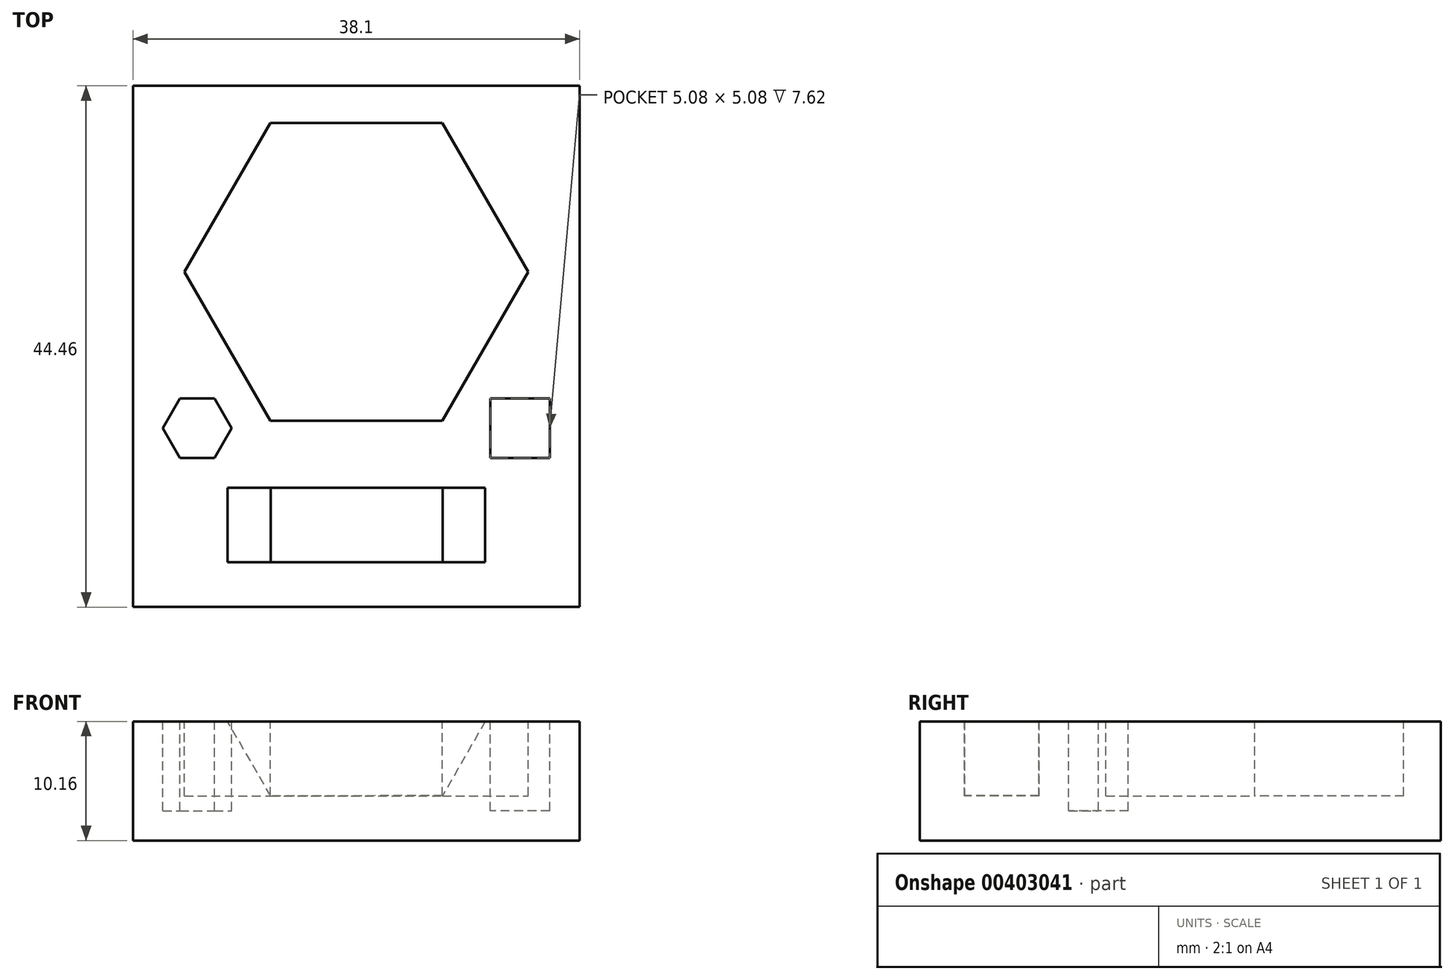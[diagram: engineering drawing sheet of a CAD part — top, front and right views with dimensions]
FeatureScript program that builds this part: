
annotation { "Feature Type Name" : "Feature", "Feature Type Description" : "" }
export const myFeature = defineFeature(function(context is Context, id is Id, definition is map)
    precondition{}
    {
        {
            var Q0;
            Q0=qCreatedBy(makeId("Top.planeOp"),FACE);
            var sketch = newSketch(context, id + "F0", { "sketchPlane" : qUnion([Q0])});
            skLineSegment(sketch, "E0.bottom", {"start": v(19.05, 22.23) * mm, "end": v(-19.05, 22.23) * mm});
            skLineSegment(sketch, "E0.top", {"start": v(19.05, -22.23) * mm, "end": v(-19.05, -22.23) * mm});
            skLineSegment(sketch, "E0.left", {"start": v(19.05, 22.23) * mm, "end": v(19.05, -22.23) * mm});
            skLineSegment(sketch, "E0.right", {"start": v(-19.05, 22.23) * mm, "end": v(-19.05, -22.23) * mm});
            skPoint(sketch, "E0.middle", {"position": v(0, 0) * mm});
            skSolve(sketch);
        }
        {
            var Q0;
            Q0 = qSketchRegion(id + "F0", true);
            extrude(context, id + "F1", {"entities" : qUnion([Q0]), "depth" : 10.16 * mm});
        }
        {
            var Q0;
            Q0=makeQuery(id+"F1.opExtrude","CAP_FACE",FACE,{"disambiguationData":[OSD([sQuery(id+"F0.wireOp",EDGE,"E0.bottom"),sQuery(id+"F0.wireOp",EDGE,"E0.top"),sQuery(id+"F0.wireOp",EDGE,"E0.left"),sQuery(id+"F0.wireOp",EDGE,"E0.right")])],"isStart":false});
            var sketch = newSketch(context, id + "F2", { "sketchPlane" : qUnion([Q0])});
            skCircle(sketch, "E1.cCircle", {"center": v(0, 6.35) * mm, "radius": 12.7 * mm, "construction": true});
            skLineSegment(sketch, "E1.0", {"start": v(7.33, 19.05) * mm, "end": v(14.66, 6.35) * mm});
            skLineSegment(sketch, "E1.1", {"start": v(14.66, 6.35) * mm, "end": v(7.33, -6.35) * mm});
            skLineSegment(sketch, "E1.2", {"start": v(7.33, -6.35) * mm, "end": v(-7.33, -6.35) * mm});
            skLineSegment(sketch, "E1.3", {"start": v(-7.33, -6.35) * mm, "end": v(-14.66, 6.35) * mm});
            skLineSegment(sketch, "E1.4", {"start": v(-14.66, 6.35) * mm, "end": v(-7.33, 19.05) * mm});
            skLineSegment(sketch, "E1.5", {"start": v(-7.33, 19.05) * mm, "end": v(7.33, 19.05) * mm});
            skPoint(sketch, "E1.0.midPoint", {"position": v(11, 12.7) * mm});
            skSolve(sketch);
        }
        {
            var Q0;
            Q0 = qSketchRegion(id + "F2", true);
            extrude(context, id + "F3", {"entities" : qUnion([Q0]), "operationType" : NewBodyOperationType.REMOVE, "oppositeDirection" : true, "depth" : 6.35 * mm});
        }
        {
            var Q0;
            Q0=qCreatedBy(makeId("Front.planeOp"),FACE);
            cPlane(context, id + "F4", {"entities" : qUnion([Q0]), "cplaneType" : CPlaneType.OFFSET, "offset" : 15.24 * mm, "width" : 152.4 * mm, "height" : 152.4 * mm});
        }
        {
            var Q0;
            Q0=qCreatedBy(id+"F4.planeOp",FACE);
            var sketch = newSketch(context, id + "F5", { "sketchPlane" : qUnion([Q0])});
            skCircle(sketch, "E2.cCircle", {"center": v(0, 16.51) * mm, "radius": 12.7 * mm, "construction": true});
            skLineSegment(sketch, "E2.0", {"start": v(14.66, 16.55) * mm, "end": v(7.36, 3.83) * mm});
            skLineSegment(sketch, "E2.1", {"start": v(7.36, 3.83) * mm, "end": v(-7.3, 3.8) * mm});
            skLineSegment(sketch, "E2.2", {"start": v(-7.3, 3.8) * mm, "end": v(-14.66, 16.47) * mm});
            skLineSegment(sketch, "E2.3", {"start": v(-14.66, 16.47) * mm, "end": v(-7.36, 29.2) * mm});
            skLineSegment(sketch, "E2.4", {"start": v(-7.36, 29.2) * mm, "end": v(7.3, 29.23) * mm});
            skLineSegment(sketch, "E2.5", {"start": v(7.3, 29.23) * mm, "end": v(14.66, 16.55) * mm});
            skPoint(sketch, "E2.0.midPoint", {"position": v(11.01, 10.19) * mm});
            skSolve(sketch);
        }
        {
            var Q0;
            Q0 = qSketchRegion(id + "F5", true);
            extrude(context, id + "F6", {"entities" : qUnion([Q0]), "operationType" : NewBodyOperationType.REMOVE, "oppositeDirection" : true, "depth" : 3.17 * mm, "hasSecondDirection" : true, "secondDirectionOppositeDirection" : false, "secondDirectionDepth" : 3.17 * mm});
        }
        {
            var Q0;
            Q0=makeQuery(id+"F1.opExtrude","CAP_FACE",FACE,{"disambiguationData":[OSD([sQuery(id+"F0.wireOp",EDGE,"E0.bottom"),sQuery(id+"F0.wireOp",EDGE,"E0.top"),sQuery(id+"F0.wireOp",EDGE,"E0.left"),sQuery(id+"F0.wireOp",EDGE,"E0.right")])],"isStart":false});
            var sketch = newSketch(context, id + "F7", { "sketchPlane" : qUnion([Q0])});
            skCircle(sketch, "E3.cCircle", {"center": v(-13.58, -6.99) * mm, "radius": 2.54 * mm, "construction": true});
            skLineSegment(sketch, "E3.0", {"start": v(-12.11, -4.45) * mm, "end": v(-10.64, -6.99) * mm});
            skLineSegment(sketch, "E3.1", {"start": v(-10.64, -6.99) * mm, "end": v(-12.11, -9.52) * mm});
            skLineSegment(sketch, "E3.2", {"start": v(-12.11, -9.52) * mm, "end": v(-15.04, -9.52) * mm});
            skLineSegment(sketch, "E3.3", {"start": v(-15.04, -9.52) * mm, "end": v(-16.5, -6.99) * mm});
            skLineSegment(sketch, "E3.4", {"start": v(-16.51, -6.99) * mm, "end": v(-15.04, -4.45) * mm});
            skLineSegment(sketch, "E3.5", {"start": v(-15.04, -4.45) * mm, "end": v(-12.11, -4.45) * mm});
            skPoint(sketch, "E3.0.midPoint", {"position": v(-11.38, -5.72) * mm});
            skSolve(sketch);
        }
        {
            var Q0;
            Q0 = qSketchRegion(id + "F7", true);
            extrude(context, id + "F8", {"entities" : qUnion([Q0]), "operationType" : NewBodyOperationType.REMOVE, "oppositeDirection" : true, "depth" : 7.62 * mm});
        }
        {
            var Q0;
            Q0=makeQuery(id+"F1.opExtrude","CAP_FACE",FACE,{"disambiguationData":[OSD([sQuery(id+"F0.wireOp",EDGE,"E0.bottom"),sQuery(id+"F0.wireOp",EDGE,"E0.top"),sQuery(id+"F0.wireOp",EDGE,"E0.left"),sQuery(id+"F0.wireOp",EDGE,"E0.right")])],"isStart":false});
            var sketch = newSketch(context, id + "F9", { "sketchPlane" : qUnion([Q0])});
            skLineSegment(sketch, "E4.bottom", {"start": v(16.51, -4.44) * mm, "end": v(11.43, -4.45) * mm});
            skLineSegment(sketch, "E4.top", {"start": v(16.51, -9.53) * mm, "end": v(11.43, -9.53) * mm});
            skLineSegment(sketch, "E4.left", {"start": v(16.51, -4.45) * mm, "end": v(16.51, -9.53) * mm});
            skLineSegment(sketch, "E4.right", {"start": v(11.43, -4.45) * mm, "end": v(11.43, -9.53) * mm});
            skPoint(sketch, "E4.middle", {"position": v(13.97, -6.99) * mm});
            skSolve(sketch);
        }
        {
            var Q0;
            Q0 = qSketchRegion(id + "F9", true);
            extrude(context, id + "F10", {"entities" : qUnion([Q0]), "operationType" : NewBodyOperationType.REMOVE, "oppositeDirection" : true, "depth" : 7.62 * mm});
        }
    });
